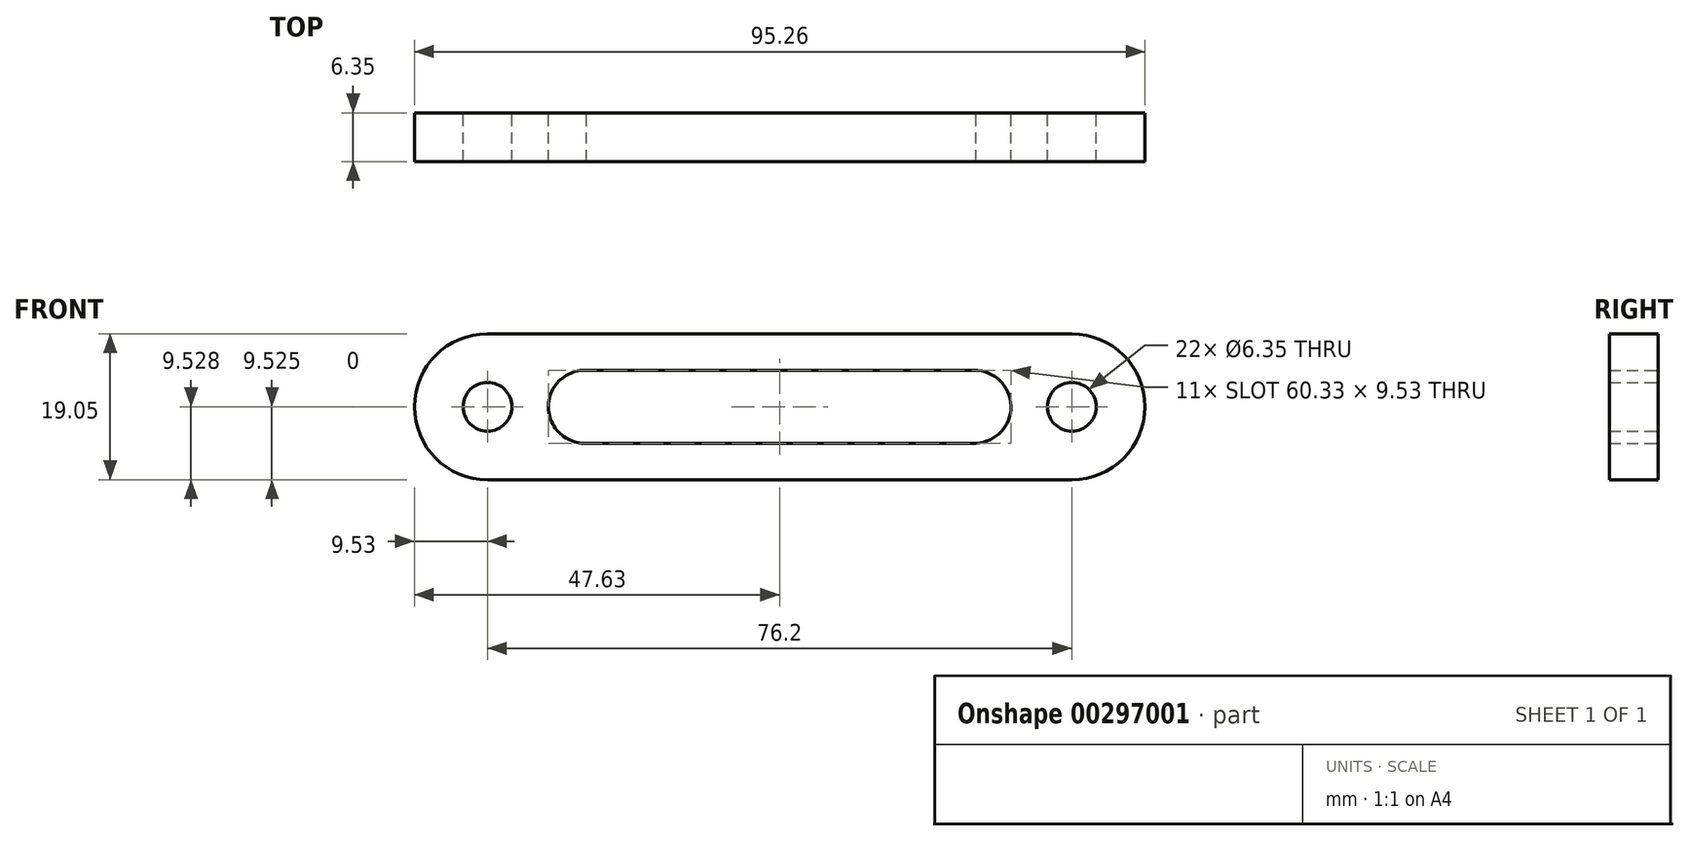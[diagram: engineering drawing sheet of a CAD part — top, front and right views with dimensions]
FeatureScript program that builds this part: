
annotation { "Feature Type Name" : "Feature", "Feature Type Description" : "" }
export const myFeature = defineFeature(function(context is Context, id is Id, definition is map)
    precondition{}
    {
        {
            var Q0;
            Q0=qCreatedBy(makeId("Front.planeOp"),FACE);
            var sketch = newSketch(context, id + "F0", { "sketchPlane" : qUnion([Q0])});
            skLineSegment(sketch, "E0", {"start": v(0, 0) * mm, "end": v(76.2, 0) * mm});
            skLineSegment(sketch, "E1", {"start": v(0, -19.05) * mm, "end": v(76.2, -19.05) * mm});
            skArc(sketch, "E2", {"start": v(0, 0) * mm, "mid": v(-9.52, -9.52) * mm, "end": v(0, -19.05) * mm});
            skArc(sketch, "E3", {"start": v(76.2, 0) * mm, "mid": v(85.72, -9.52) * mm, "end": v(76.2, -19.05) * mm});
            skLineSegment(sketch, "E4", {"start": v(12.7, -4.76) * mm, "end": v(63.5, -4.76) * mm});
            skLineSegment(sketch, "E5", {"start": v(12.92, -14.28) * mm, "end": v(63.72, -14.28) * mm});
            skArc(sketch, "E6", {"start": v(12.7, -4.76) * mm, "mid": v(7.94, -9.64) * mm, "end": v(12.92, -14.28) * mm});
            skArc(sketch, "E7", {"start": v(63.5, -4.76) * mm, "mid": v(68.26, -9.41) * mm, "end": v(63.72, -14.28) * mm});
            skCircle(sketch, "E8", {"center": v(0, -9.53) * mm, "radius": 3.18 * mm});
            skCircle(sketch, "E9", {"center": v(76.2, -9.53) * mm, "radius": 3.18 * mm});
            skSolve(sketch);
        }
        {
            var Q0;
            Q0=makeQuery(id+"F0.imprint","IMPRINT",FACE,{"disambiguationData":[TD([[makeQuery(id+"F0.imprint","IMPRINT",EDGE,{"derivedFrom":sQuery(id+"F0.wireOp",EDGE,"E0")}),-1.0]])]});
            extrude(context, id + "F1", {"entities" : qUnion([Q0]), "depth" : 6.35 * mm});
        }
    });
